# Revit family: Haworth_EncloseFrameless_Wall_Glass
name_source: partatom
category: Furniture Systems
revit_build: Autodesk Revit 2018 (Build: 20170223_1515(x64)
units: mm (PartAtom-declared; Revit-internal decimal feet)

## family parameters
Always vertical = Yes
Cut with Voids When Loaded = No
OmniClass Number = 23.25.40.14
OmniClass Title = Demountable Partitions
Part Type = Normal
Room Calculation Point = No
Round Connector Dimension = Use Diameter
Shared = Yes
Work Plane-Based = No

## types (1)
- 108" H
    Actual Height = 108 "
    Assembly Code = C1010200
    Base Height = 0.375 "
    Cap Height = 1 "
    Ceiling Mount = Yes
    Description = Wall - Glass
    Double Glazed = No
    End of Run Finish = Haworth _ Polymer _ Black
    Frame Depth = 4 "
    Frame Finish = Haworth _ Metal _ Brushed Aluminum
    Glass Finish = Haworth _ Glass _ Clear
    Glass Offset = 1.25 "
    Half Postcap Width = 0.155 "
    Height = 108 "
    Horizontal Bottom Adjuster Width = 1.25 "
    Horizontal Frame Width = 0.875 "
    Horizontal Top Adjuster Width = 2.625 "
    Horizontal Top Trim Width = 1.43 "
    Manufacturer = Haworth
    Material Options = http://surfaces.haworth.com
    Max. Height = 144 "
    Min. Height = 24 "
    Min/Max Height = 24-144 in.
    Min/Max Width = 12in Min, Verify Max
    Model = Haworth - Enclose Frameless
    Panel Depth = 0.4 "
    Panel Height = 103.25 "
    Revision Number = 3
    Single Glazed = Yes
    Size = Verify Final Dim. w/ Haworth
    Sustainability Info = http://www.haworth.com
    URL = www.haworth.com
    URL - Product = http://www.haworth.com
    Vertical Frame Width = 0.875 "
    Warranty = http://www.haworth.com

## geometry (parser evidence)
native form markers: Sweep x9
no freeform markers — native parametric forms only
